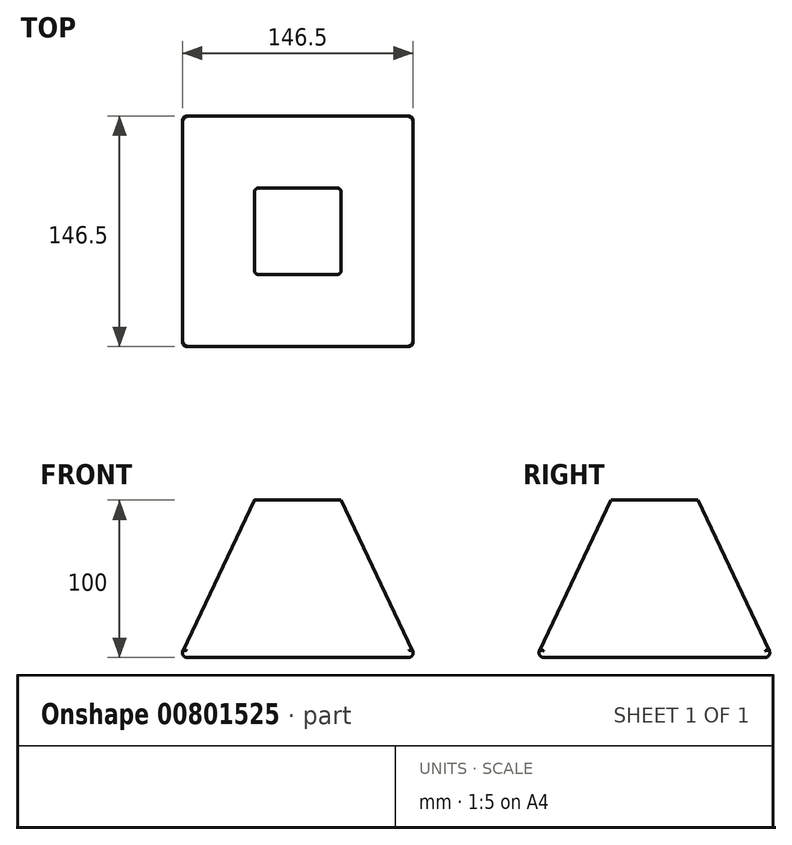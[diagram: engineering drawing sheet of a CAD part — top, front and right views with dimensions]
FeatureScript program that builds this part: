
annotation { "Feature Type Name" : "Feature", "Feature Type Description" : "" }
export const myFeature = defineFeature(function(context is Context, id is Id, definition is map)
    precondition{}
    {
        {
            var Q0;
            Q0=qCreatedBy(makeId("Top.planeOp"),FACE);
            var sketch = newSketch(context, id + "F0", { "sketchPlane" : qUnion([Q0])});
            skLineSegment(sketch, "E0.bottom", {"start": v(75, -75) * mm, "end": v(-75, -75) * mm});
            skLineSegment(sketch, "E0.top", {"start": v(75, 75) * mm, "end": v(-75, 75) * mm});
            skLineSegment(sketch, "E0.left", {"start": v(75, -75) * mm, "end": v(75, 75) * mm});
            skLineSegment(sketch, "E0.right", {"start": v(-75, -75) * mm, "end": v(-75, 75) * mm});
            skPoint(sketch, "E0.middle", {"position": v(0, 0) * mm});
            skSolve(sketch);
        }
        {
            var Q0;
            Q0=makeQuery(id+"F0.imprint","IMPRINT",FACE,{"disambiguationData":[TD([[makeQuery(id+"F0.imprint","IMPRINT",EDGE,{"derivedFrom":sQuery(id+"F0.wireOp",EDGE,"E0.bottom")}),-1.0]])]});
            cPlane(context, id + "F1", {"entities" : qUnion([Q0]), "cplaneType" : CPlaneType.OFFSET, "offset" : 100 * mm, "width" : 152.4 * mm, "height" : 152.4 * mm});
        }
        {
            var Q0;
            Q0=qCreatedBy(id+"F1.planeOp",FACE);
            var sketch = newSketch(context, id + "F2", { "sketchPlane" : qUnion([Q0])});
            skLineSegment(sketch, "E1.bottom", {"start": v(0, 0) * mm, "end": v(0, 0) * mm});
            skLineSegment(sketch, "E1.top", {"start": v(0, 0) * mm, "end": v(0, 0) * mm});
            skLineSegment(sketch, "E1.left", {"start": v(0, 0) * mm, "end": v(0, 0) * mm});
            skLineSegment(sketch, "E1.right", {"start": v(0, 0) * mm, "end": v(0, 0) * mm});
            skPoint(sketch, "E1.middle", {"position": v(0, 0) * mm});
            skLineSegment(sketch, "E2.bottom", {"start": v(27.5, -27.5) * mm, "end": v(-27.5, -27.5) * mm});
            skLineSegment(sketch, "E2.top", {"start": v(27.5, 27.5) * mm, "end": v(-27.5, 27.5) * mm});
            skLineSegment(sketch, "E2.left", {"start": v(27.5, -27.5) * mm, "end": v(27.5, 27.5) * mm});
            skLineSegment(sketch, "E2.right", {"start": v(-27.5, -27.5) * mm, "end": v(-27.5, 27.5) * mm});
            skSolve(sketch);
        }
        {
            var Q0;
            Q0 = qSketchRegion(id + "F2", true);
            var Q1;
            Q1 = qSketchRegion(id + "F0", true);
            loft(context, id + "F3", {"sheetProfilesArray" : [{ "sheetProfileEntities" : qUnion([Q0]) }, { "sheetProfileEntities" : qUnion([Q1]) }]});
        }
        {
            var Q0;
            Q0=makeQuery(id+"F3.opLoft","CAP_FACE",FACE,{"disambiguationData":[OSD([makeQuery(id+"F0.imprint","IMPRINT",FACE,{"disambiguationData":[TD([[makeQuery(id+"F0.imprint","IMPRINT",EDGE,{"derivedFrom":sQuery(id+"F0.wireOp",EDGE,"E0.bottom")}),-1.0]])]})])],"isStart":true});
            var sketch = newSketch(context, id + "F4", { "sketchPlane" : qUnion([Q0])});
            skLineSegment(sketch, "E3.bottom", {"start": v(-10, 75) * mm, "end": v(10, 75) * mm});
            skLineSegment(sketch, "E3.top", {"start": v(-10, 0) * mm, "end": v(10, 0) * mm});
            skLineSegment(sketch, "E3.left", {"start": v(10, 75) * mm, "end": v(10, 0) * mm});
            skLineSegment(sketch, "E3.right", {"start": v(-10, 75) * mm, "end": v(-10, 0) * mm});
            skSolve(sketch);
        }
        {
            var Q0;
            Q0=makeQuery(id+"FRhxWNlymH17jAR_1.boolean.opBoolean","MERGE",FACE,{"derivedFrom":[makeQuery(id+"F3.opLoft","CAP_FACE",FACE,{"disambiguationData":[OSD([makeQuery(id+"F2.imprint","IMPRINT",FACE,{"disambiguationData":[TD([[makeQuery(id+"F2.imprint","IMPRINT",EDGE,{"derivedFrom":sQuery(id+"F2.wireOp",EDGE,"E2.bottom")}),-1.0]])]})])],"isStart":true}),makeQuery(id+"FRhxWNlymH17jAR_1.opExtrude","CAP_FACE",FACE,{"disambiguationData":[OSD([sQuery(id+"F4.wireOp",EDGE,"E3.bottom"),sQuery(id+"F4.wireOp",EDGE,"E3.top"),sQuery(id+"F4.wireOp",EDGE,"E3.left"),sQuery(id+"F4.wireOp",EDGE,"E3.right")])],"isStart":false})]});
            var sketch = newSketch(context, id + "F5", { "sketchPlane" : qUnion([Q0])});
            skSolve(sketch);
        }
        {
            var Q0;
            Q0=makeQuery(id+"F3.opLoft","SWEPT_EDGE",EDGE,{"disambiguationData":[OSD([sQuery(id+"F0.wireOp",EDGE,"E0.bottom"),sQuery(id+"F0.wireOp",EDGE,"E0.left"),sQuery(id+"F2.wireOp",EDGE,"E2.bottom"),sQuery(id+"F2.wireOp",EDGE,"E2.left")])]});
            var Q1;
            Q1=makeQuery(id+"F3.opLoft","SWEPT_EDGE",EDGE,{"disambiguationData":[OSD([sQuery(id+"F0.wireOp",EDGE,"E0.top"),sQuery(id+"F0.wireOp",EDGE,"E0.left"),sQuery(id+"F2.wireOp",EDGE,"E2.top"),sQuery(id+"F2.wireOp",EDGE,"E2.left")])]});
            var Q2;
            Q2=makeQuery(id+"F3.opLoft","SWEPT_EDGE",EDGE,{"disambiguationData":[OSD([sQuery(id+"F0.wireOp",EDGE,"E0.bottom"),sQuery(id+"F0.wireOp",EDGE,"E0.right"),sQuery(id+"F2.wireOp",EDGE,"E2.bottom"),sQuery(id+"F2.wireOp",EDGE,"E2.right")])]});
            var Q3;
            Q3=makeQuery(id+"F3.opLoft","SWEPT_EDGE",EDGE,{"disambiguationData":[OSD([sQuery(id+"F0.wireOp",EDGE,"E0.top"),sQuery(id+"F0.wireOp",EDGE,"E0.right"),sQuery(id+"F2.wireOp",EDGE,"E2.top"),sQuery(id+"F2.wireOp",EDGE,"E2.right")])]});
            var Q4;
            Q4=makeQuery(id+"F3.opLoft","MID_CAP_EDGE",EDGE,{"disambiguationData":[OSD([sQuery(id+"F0.wireOp",EDGE,"E0.bottom"),sQuery(id+"F0.wireOp",EDGE,"E0.top"),sQuery(id+"F0.wireOp",EDGE,"E0.right")])],"capPos":1.0});
            var Q5;
            Q5=makeQuery(id+"F3.opLoft","MID_CAP_EDGE",EDGE,{"disambiguationData":[OSD([sQuery(id+"F0.wireOp",EDGE,"E0.bottom"),sQuery(id+"F0.wireOp",EDGE,"E0.left"),sQuery(id+"F0.wireOp",EDGE,"E0.right")])],"capPos":1.0});
            var Q6;
            Q6=makeQuery(id+"F3.opLoft","MID_CAP_EDGE",EDGE,{"disambiguationData":[OSD([sQuery(id+"F0.wireOp",EDGE,"E0.bottom"),sQuery(id+"F0.wireOp",EDGE,"E0.top"),sQuery(id+"F0.wireOp",EDGE,"E0.left")])],"capPos":1.0});
            var Q7;
            Q7=makeQuery(id+"F3.opLoft","MID_CAP_EDGE",EDGE,{"disambiguationData":[OSD([sQuery(id+"F0.wireOp",EDGE,"E0.top"),sQuery(id+"F0.wireOp",EDGE,"E0.left"),sQuery(id+"F0.wireOp",EDGE,"E0.right")])],"capPos":1.0});
            fillet(context, id + "F6", {"entities" : qUnion([Q0, Q1, Q2, Q3, Q4, Q5, Q6, Q7]), "radius" : 3 * mm, "tangentPropagation" : true, "allowEdgeOverflow" : false});
        }
    });
